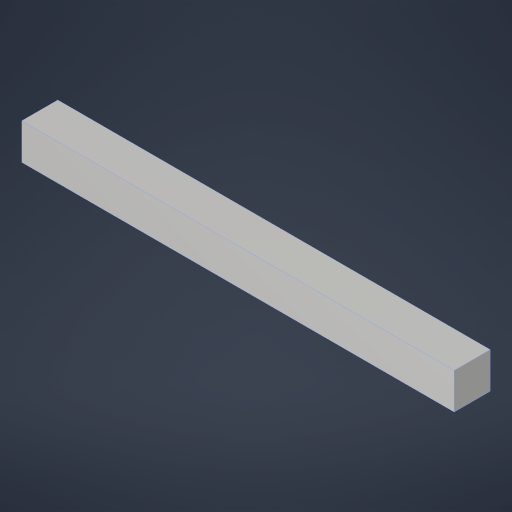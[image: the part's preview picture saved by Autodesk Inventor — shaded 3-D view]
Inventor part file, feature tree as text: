
AUTODESK INVENTOR PART (.ipt)
format: ipt  version: 2024.2 (Build 282272000, 272)  size: 158,208 bytes
history: native  units: in
note: dims shown in document units (in); Inventor stores cm internally (conversion verified against a paired STEP export)
features: extrude x1, sketch x1
ambient origin geometry x8: Origin, YZ Plane, XZ Plane, XY Plane, X Axis, Y Axis, Z Axis, Center Point
bodies: Solid1 (feature_tree)
feature tree (2):
  extrude  "Extrusion1"  Depth=2.0in
  sketch  "Sketch1"  dims[d0=2.0in d1=2.0in d2=24.0in d3=0.0in]
